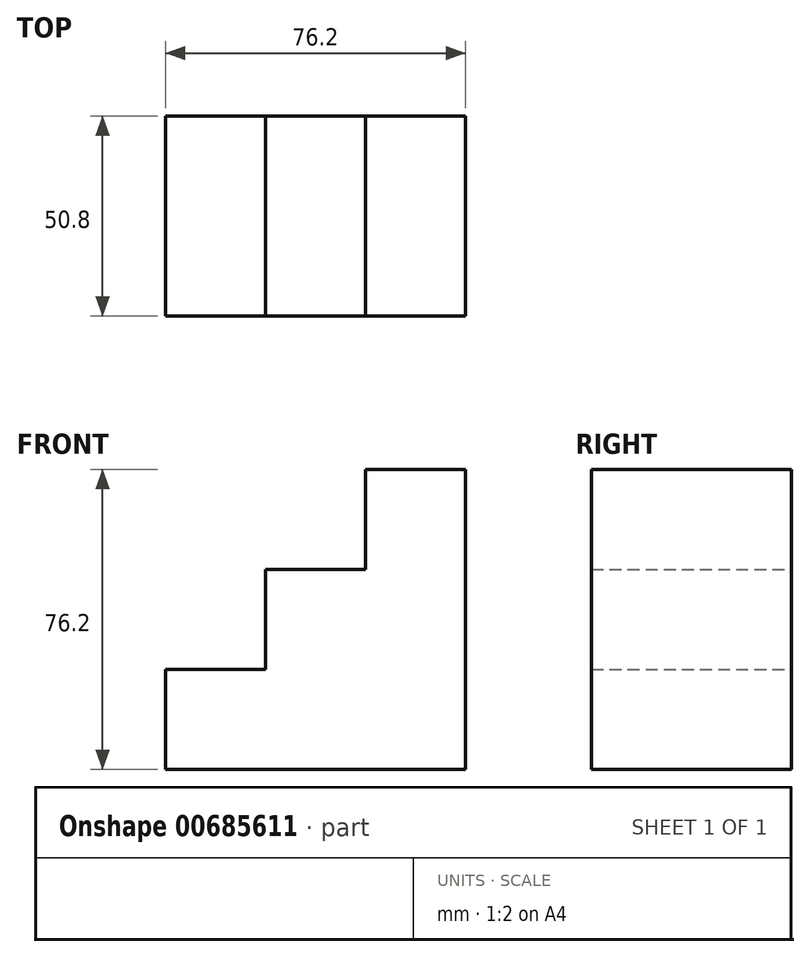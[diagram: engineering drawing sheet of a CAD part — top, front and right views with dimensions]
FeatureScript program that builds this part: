
annotation { "Feature Type Name" : "Feature", "Feature Type Description" : "" }
export const myFeature = defineFeature(function(context is Context, id is Id, definition is map)
    precondition{}
    {
        {
            var Q0;
            Q0=qCreatedBy(makeId("Front.planeOp"),FACE);
            var sketch = newSketch(context, id + "F0", { "sketchPlane" : qUnion([Q0])});
            skLineSegment(sketch, "E0", {"start": v(-21.86, 0) * mm, "end": v(54.34, 0) * mm});
            skLineSegment(sketch, "E1", {"start": v(54.34, 0) * mm, "end": v(54.34, 76.2) * mm});
            skLineSegment(sketch, "E2", {"start": v(54.34, 76.2) * mm, "end": v(28.94, 76.2) * mm});
            skLineSegment(sketch, "E3", {"start": v(28.94, 76.2) * mm, "end": v(28.94, 50.8) * mm});
            skLineSegment(sketch, "E4", {"start": v(28.94, 50.8) * mm, "end": v(3.54, 50.8) * mm});
            skLineSegment(sketch, "E5", {"start": v(3.54, 50.8) * mm, "end": v(3.54, 25.4) * mm});
            skLineSegment(sketch, "E6", {"start": v(3.54, 25.4) * mm, "end": v(-21.86, 25.4) * mm});
            skLineSegment(sketch, "E7", {"start": v(-21.86, 25.4) * mm, "end": v(-21.86, 0) * mm});
            skSolve(sketch);
        }
        {
            var Q0;
            Q0 = qSketchRegion(id + "F0", true);
            extrude(context, id + "F1", {"entities" : qUnion([Q0]), "depth" : 50.8 * mm, "offsetDistance" : 25.4 * mm});
        }
    });
